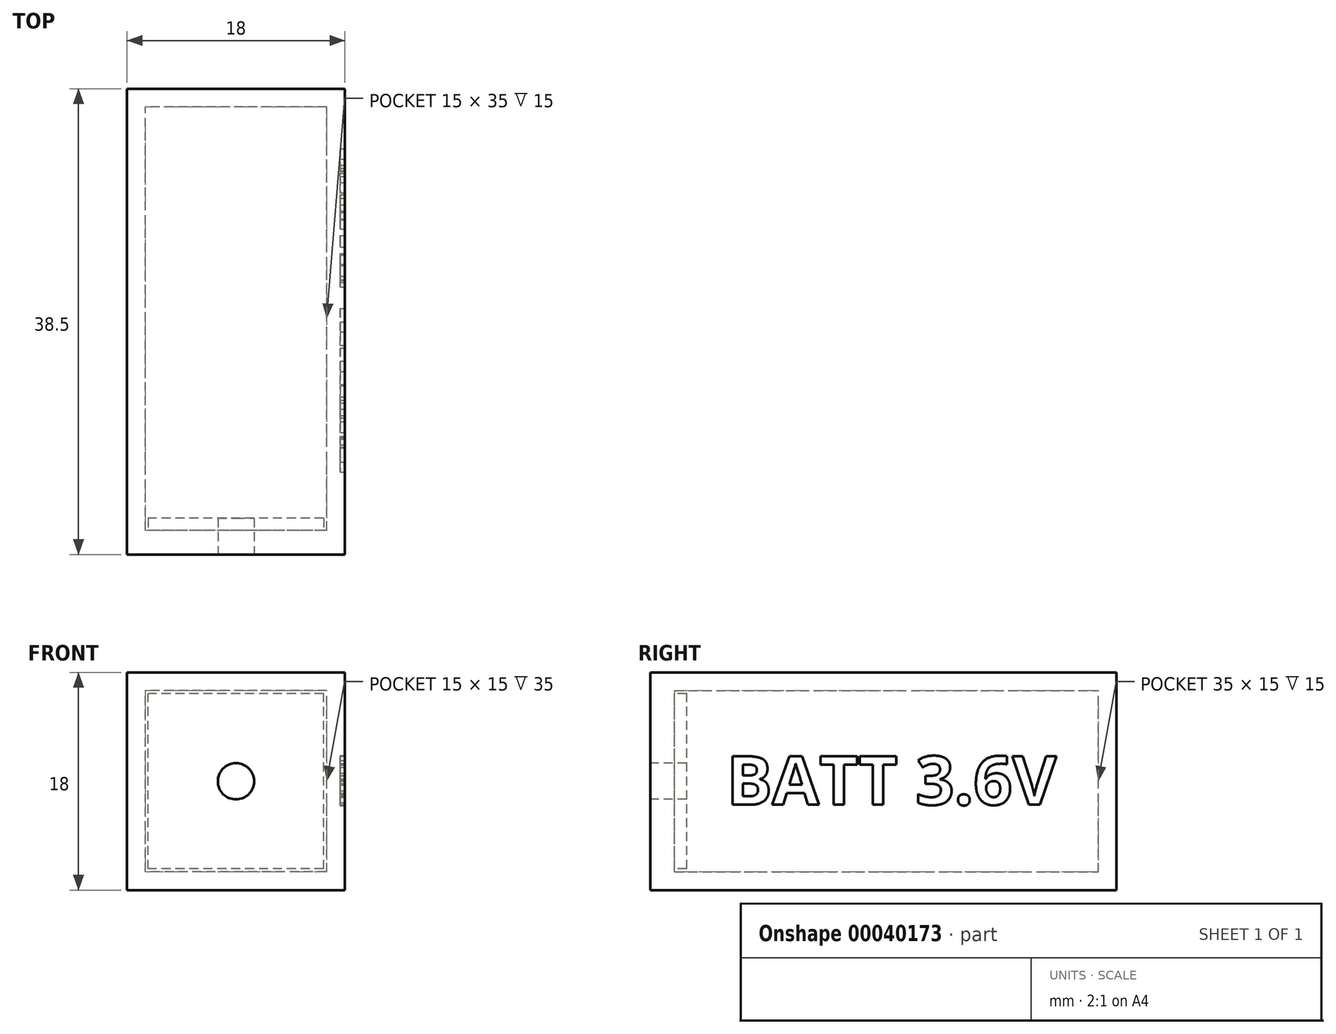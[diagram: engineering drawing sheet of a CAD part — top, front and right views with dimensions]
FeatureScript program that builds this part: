
annotation { "Feature Type Name" : "Feature", "Feature Type Description" : "" }
export const myFeature = defineFeature(function(context is Context, id is Id, definition is map)
    precondition{}
    {
        {
            var Q0;
            Q0=qCreatedBy(makeId("Front.planeOp"),FACE);
            var sketch = newSketch(context, id + "F0", { "sketchPlane" : qUnion([Q0])});
            skLineSegment(sketch, "E0.rect.bottom", {"start": v(9, -9) * mm, "end": v(-9, -9) * mm});
            skLineSegment(sketch, "E0.rect.top", {"start": v(9, 9) * mm, "end": v(-9, 9) * mm});
            skLineSegment(sketch, "E0.rect.left", {"start": v(9, -9) * mm, "end": v(9, 9) * mm});
            skLineSegment(sketch, "E0.rect.right", {"start": v(-9, -9) * mm, "end": v(-9, 9) * mm});
            skPoint(sketch, "E0.rect.middle", {"position": v(0, 0) * mm});
            skSolve(sketch);
        }
        {
            var Q0;
            Q0=makeQuery(id+"F0.imprint","IMPRINT",FACE,{"disambiguationData":[TD([[makeQuery(id+"F0.imprint","IMPRINT",EDGE,{"derivedFrom":sQuery(id+"F0.wireOp",EDGE,"E0.rect.bottom")}),-1.0]])]});
            extrude(context, id + "F1", {"entities" : qUnion([Q0]), "depth" : 36.5 * mm});
        }
        {
            var Q0;
            Q0=makeQuery(id+"F1.opExtrude","CAP_FACE",FACE,{"disambiguationData":[OSD([sQuery(id+"F0.wireOp",EDGE,"E0.rect.bottom"),sQuery(id+"F0.wireOp",EDGE,"E0.rect.top"),sQuery(id+"F0.wireOp",EDGE,"E0.rect.left"),sQuery(id+"F0.wireOp",EDGE,"E0.rect.right")])],"isStart":false});
            shell(context, id + "F2", {"entities" : qUnion([Q0]), "thickness" : 1.5 * mm});
        }
        {
            var Q0;
            Q0=makeQuery(id+"F1.opExtrude","CAP_FACE",FACE,{"disambiguationData":[OSD([sQuery(id+"F0.wireOp",EDGE,"E0.rect.bottom"),sQuery(id+"F0.wireOp",EDGE,"E0.rect.top"),sQuery(id+"F0.wireOp",EDGE,"E0.rect.left"),sQuery(id+"F0.wireOp",EDGE,"E0.rect.right")])],"isStart":false});
            var sketch = newSketch(context, id + "F3", { "sketchPlane" : qUnion([Q0])});
            skLineSegment(sketch, "E1.0", {"start": v(-7.25, -7.25) * mm, "end": v(-7.25, 7.25) * mm});
            skLineSegment(sketch, "E1.1", {"start": v(7.25, -7.25) * mm, "end": v(-7.25, -7.25) * mm});
            skLineSegment(sketch, "E1.2", {"start": v(7.25, -7.25) * mm, "end": v(7.25, 7.25) * mm});
            skLineSegment(sketch, "E1.3", {"start": v(7.25, 7.25) * mm, "end": v(-7.25, 7.25) * mm});
            skSolve(sketch);
        }
        {
            var Q0;
            Q0=makeQuery(id+"F3.imprint","IMPRINT",FACE,{"disambiguationData":[TD([[makeQuery(id+"F3.imprint","IMPRINT",EDGE,{"derivedFrom":sQuery(id+"F3.wireOp",EDGE,"E1.0")}),-1.0]])]});
            extrude(context, id + "F4", {"entities" : qUnion([Q0]), "oppositeDirection" : true, "depth" : 1 * mm});
        }
        {
            var Q0;
            Q0=makeQuery(id+"F4.opExtrude","CAP_FACE",FACE,{"disambiguationData":[OSD([sQuery(id+"F3.wireOp",EDGE,"E1.0"),sQuery(id+"F3.wireOp",EDGE,"E1.1"),sQuery(id+"F3.wireOp",EDGE,"E1.2"),sQuery(id+"F3.wireOp",EDGE,"E1.3")])],"isStart":true});
            var sketch = newSketch(context, id + "F5", { "sketchPlane" : qUnion([Q0])});
            skLineSegment(sketch, "E2.0", {"start": v(9, 9) * mm, "end": v(-9, 9) * mm});
            skLineSegment(sketch, "E3.0", {"start": v(-9, -9) * mm, "end": v(-9, 9) * mm});
            skLineSegment(sketch, "E4.0", {"start": v(9, -9) * mm, "end": v(-9, -9) * mm});
            skLineSegment(sketch, "E5.0", {"start": v(9, -9) * mm, "end": v(9, 9) * mm});
            skSolve(sketch);
        }
        {
            var Q0;
            Q0=makeQuery(id+"F5.imprint","IMPRINT",FACE,{"disambiguationData":[TD([[makeQuery(id+"F5.imprint","IMPRINT",EDGE,{"derivedFrom":makeQuery(id+"F4.opExtrude","CAP_EDGE",EDGE,{"disambiguationData":[OSD([sQuery(id+"F3.wireOp",EDGE,"E1.0")])],"isStart":true})}),-1.0]])]});
            var sketch = newSketch(context, id + "F6", { "sketchPlane" : qUnion([Q0])});
            skLineSegment(sketch, "E6.0.0", {"start": v(9, -9) * mm, "end": v(9, 9) * mm});
            skLineSegment(sketch, "E6.0.1", {"start": v(9, 9) * mm, "end": v(-9, 9) * mm});
            skLineSegment(sketch, "E6.0.2", {"start": v(-9, 9) * mm, "end": v(-9, -9) * mm});
            skLineSegment(sketch, "E6.0.3", {"start": v(-9, -9) * mm, "end": v(9, -9) * mm});
            skLineSegment(sketch, "E7.bottom", {"start": v(-9, 9) * mm, "end": v(9, 9) * mm});
            skLineSegment(sketch, "E7.right", {"start": v(9, 9) * mm, "end": v(9, -9) * mm});
            skSolve(sketch);
        }
        {
            var Q0;
            Q0 = qSketchRegion(id + "F6", true);
            extrude(context, id + "F7", {"entities" : qUnion([Q0]), "operationType" : NewBodyOperationType.ADD, "depth" : 2 * mm});
        }
        {
            var Q0;
            Q0=makeQuery(id+"F7.opExtrude","CAP_FACE",FACE,{"disambiguationData":[OSD([sQuery(id+"F6.wireOp",EDGE,"E7.bottom"),sQuery(id+"F6.wireOp",EDGE,"E6.0.3"),sQuery(id+"F6.wireOp",EDGE,"E6.0.2"),sQuery(id+"F6.wireOp",EDGE,"E7.right")])],"isStart":false});
            var sketch = newSketch(context, id + "F8", { "sketchPlane" : qUnion([Q0])});
            skCircle(sketch, "E8", {"center": v(0, 0) * mm, "radius": 1.5 * mm});
            skSolve(sketch);
        }
        {
            var Q0;
            Q0=makeQuery(id+"F8.imprint","IMPRINT",FACE,{"disambiguationData":[TD([[makeQuery(id+"F8.imprint","IMPRINT",EDGE,{"derivedFrom":sQuery(id+"F8.wireOp",EDGE,"E8")}),1.0]])]});
            extrude(context, id + "F9", {"entities" : qUnion([Q0]), "operationType" : NewBodyOperationType.REMOVE, "endBound" : BoundingType.UP_TO_NEXT, "oppositeDirection" : true, "depth" : 25.4 * mm});
        }
        {
            var Q0;
            Q0=makeQuery(id+"F1.opExtrude","SWEPT_FACE",FACE,{"disambiguationData":[OSD([sQuery(id+"F0.wireOp",EDGE,"E0.rect.left")])]});
            var sketch = newSketch(context, id + "F10", { "sketchPlane" : qUnion([Q0])});
            skText(sketch, "E9", { "text": "BATT 3.6V", "fontName": "OpenSans-Bold.ttf"});
            const initialGuessF10  = {"E9": [-0.0322, -0.00194, 1, 0, 0.00404]};
            skSetInitialGuess(sketch, initialGuessF10);
            skSolve(sketch);
        }
        {
            var Q0;
            Q0 = qSketchRegion(id + "F10", true);
            extrude(context, id + "F11", {"entities" : qUnion([Q0]), "operationType" : NewBodyOperationType.REMOVE, "oppositeDirection" : true, "depth" : .4 * mm});
        }
    });
